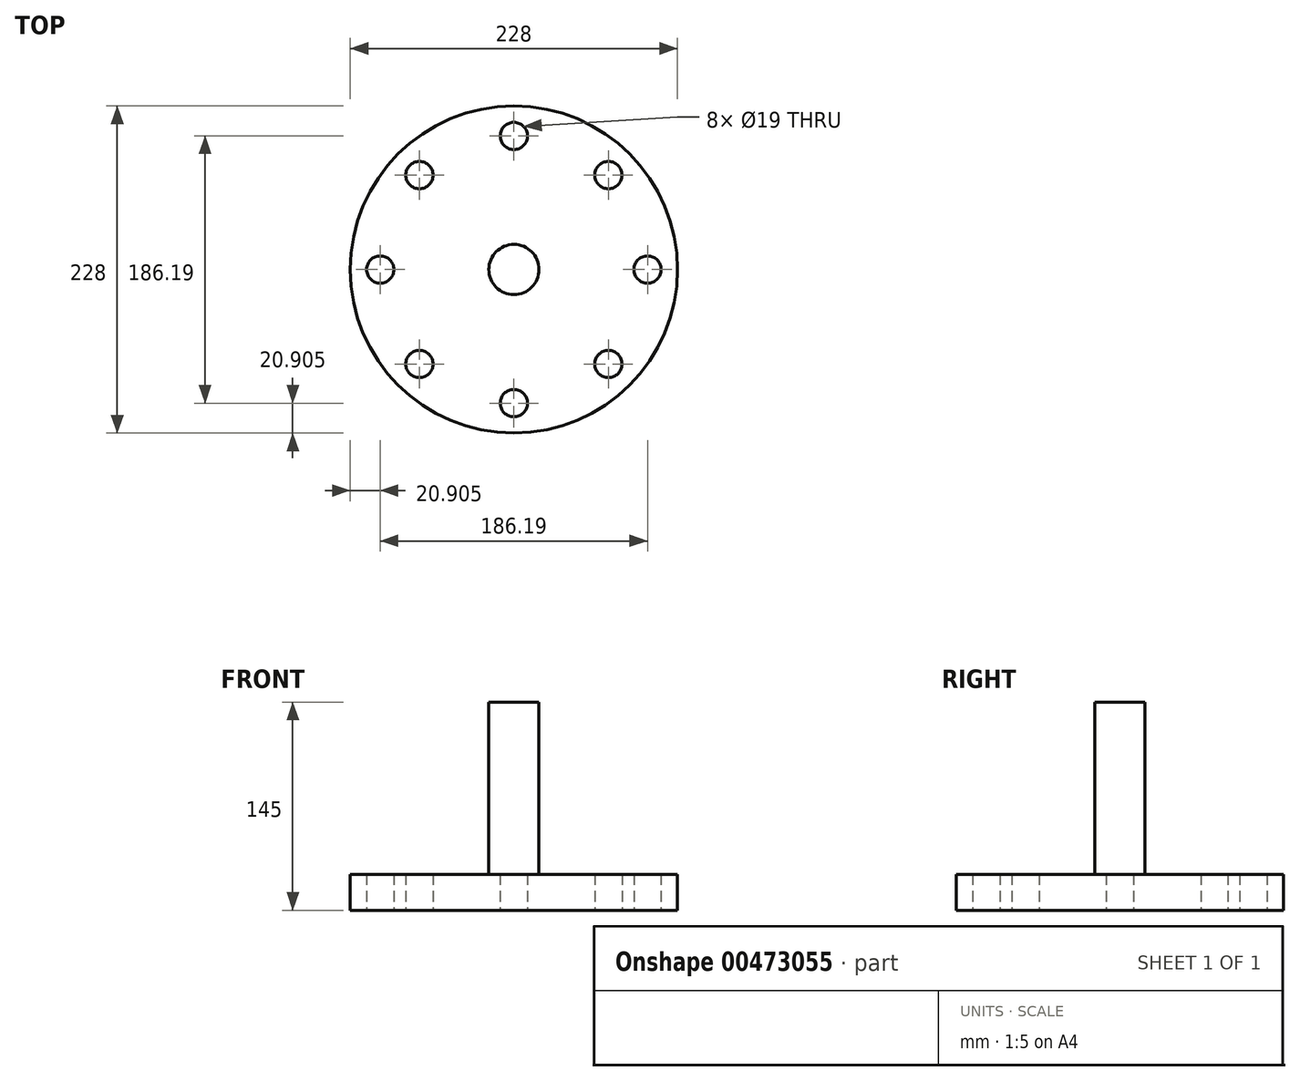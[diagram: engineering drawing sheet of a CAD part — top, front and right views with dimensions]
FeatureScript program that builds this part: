
annotation { "Feature Type Name" : "Feature", "Feature Type Description" : "" }
export const myFeature = defineFeature(function(context is Context, id is Id, definition is map)
    precondition{}
    {
        {
            var Q0;
            Q0=qCreatedBy(makeId("Top.planeOp"),FACE);
            var sketch = newSketch(context, id + "F0", { "sketchPlane" : qUnion([Q0])});
            skCircle(sketch, "E0", {"center": v(0, 0) * mm, "radius": 114 * mm});
            skCircle(sketch, "E1", {"center": v(93.1, 0) * mm, "radius": 9.5 * mm});
            skCircle(sketch, "E2.1.0", {"center": v(65.83, 65.83) * mm, "radius": 9.5 * mm});
            skCircle(sketch, "E2.2.0", {"center": v(0, 93.1) * mm, "radius": 9.5 * mm});
            skCircle(sketch, "E2.3.0", {"center": v(-65.83, 65.83) * mm, "radius": 9.5 * mm});
            skCircle(sketch, "E2.4.0", {"center": v(-93.1, 0) * mm, "radius": 9.5 * mm});
            skCircle(sketch, "E2.5.0", {"center": v(-65.83, -65.83) * mm, "radius": 9.5 * mm});
            skCircle(sketch, "E2.6.0", {"center": v(0, -93.1) * mm, "radius": 9.5 * mm});
            skCircle(sketch, "E2.7.0", {"center": v(65.83, -65.83) * mm, "radius": 9.5 * mm});
            skSolve(sketch);
        }
        {
            var Q0;
            Q0 = qSketchRegion(id + "F0", true);
            extrude(context, id + "F1", {"entities" : qUnion([Q0]), "depth" : 25 * mm});
        }
        {
            var Q0;
            Q0=makeQuery(id+"F1.opExtrude","CAP_FACE",FACE,{"disambiguationData":[OSD([sQuery(id+"F0.wireOp",EDGE,"E0"),sQuery(id+"F0.wireOp",EDGE,"E1"),sQuery(id+"F0.wireOp",EDGE,"E2.1.0"),sQuery(id+"F0.wireOp",EDGE,"E2.2.0"),sQuery(id+"F0.wireOp",EDGE,"E2.3.0"),sQuery(id+"F0.wireOp",EDGE,"E2.4.0"),sQuery(id+"F0.wireOp",EDGE,"E2.5.0"),sQuery(id+"F0.wireOp",EDGE,"E2.6.0"),sQuery(id+"F0.wireOp",EDGE,"E2.7.0")])],"isStart":false});
            var sketch = newSketch(context, id + "F2", { "sketchPlane" : qUnion([Q0])});
            skCircle(sketch, "E3", {"center": v(0, 0) * mm, "radius": 17.5 * mm});
            skSolve(sketch);
        }
        {
            var Q0;
            Q0 = qSketchRegion(id + "F2", true);
            extrude(context, id + "F3", {"entities" : qUnion([Q0]), "operationType" : NewBodyOperationType.ADD, "depth" : 120 * mm});
        }
    });
